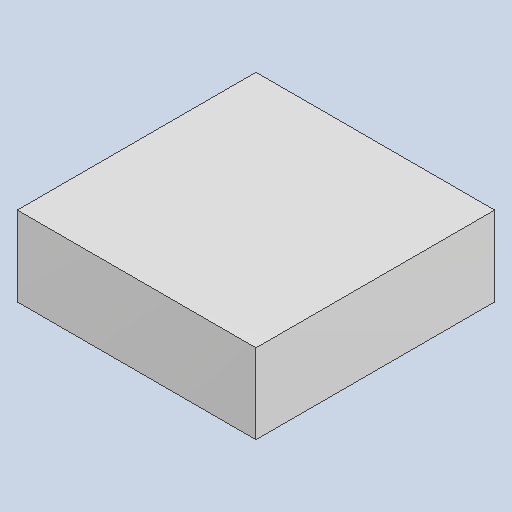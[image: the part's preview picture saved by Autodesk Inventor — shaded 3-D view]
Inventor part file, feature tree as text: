
AUTODESK INVENTOR PART (.ipt)
format: ipt  version: 2023.4 (Build 274418000, 418)  size: 79,872 bytes
history: native  units: mm
features: extrude x1
ambient origin geometry x8: Origin, YZ Plane, XZ Plane, XY Plane, X Axis, Y Axis, Z Axis, Center Point
bodies: Solid1 (feature_tree)
feature tree (1):
  extrude  "Extruded_59"  [1 undecoded]
note: 1 required parameter value undecoded (feature->parameter linkage not recoverable at this tier; creation-order binding heuristic only, values carry confidence <= 0.55)
